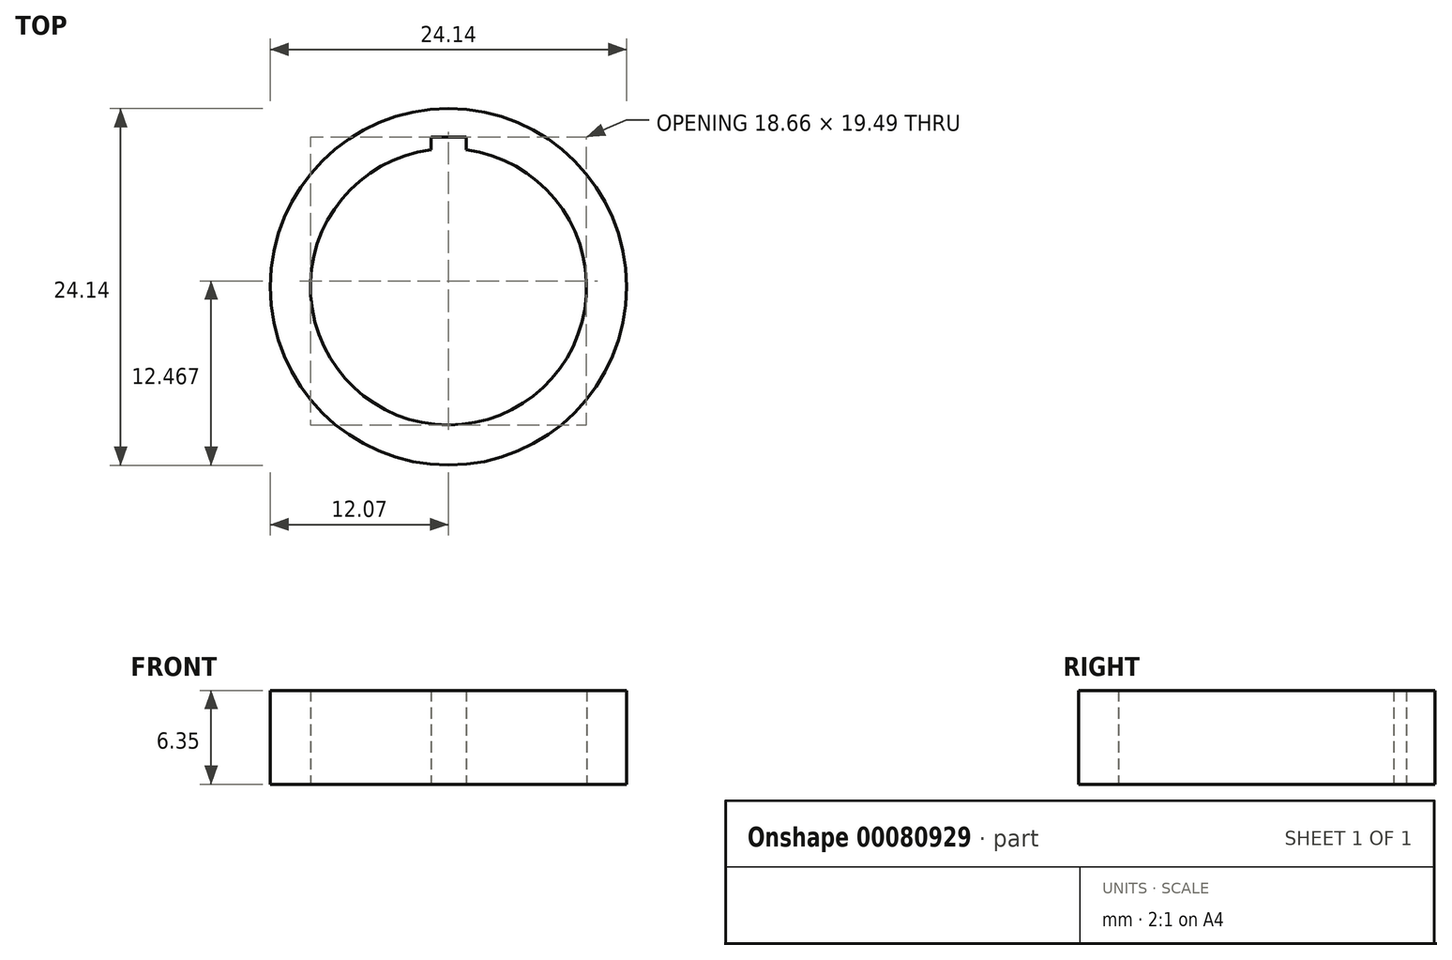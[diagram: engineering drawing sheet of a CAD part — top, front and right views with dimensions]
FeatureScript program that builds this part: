
annotation { "Feature Type Name" : "Feature", "Feature Type Description" : "" }
export const myFeature = defineFeature(function(context is Context, id is Id, definition is map)
    precondition{}
    {
        {
            var Q0;
            Q0=qCreatedBy(makeId("Top.planeOp"),FACE);
            var sketch = newSketch(context, id + "F0", { "sketchPlane" : qUnion([Q0])});
            skCircle(sketch, "E0", {"center": v(0, 0) * mm, "radius": 12.07 * mm});
            skCircle(sketch, "E1", {"center": v(0, 0) * mm, "radius": 9.35 * mm});
            skLineSegment(sketch, "E2.bottom", {"start": v(-1.2, 0) * mm, "end": v(1.2, 0) * mm});
            skLineSegment(sketch, "E2.top", {"start": v(-1.2, 10.14) * mm, "end": v(1.2, 10.14) * mm});
            skLineSegment(sketch, "E2.left", {"start": v(-1.2, 0) * mm, "end": v(-1.2, 10.14) * mm});
            skLineSegment(sketch, "E2.right", {"start": v(1.2, 0) * mm, "end": v(1.2, 10.14) * mm});
            skSolve(sketch);
        }
        {
            var Q0;
            Q0=makeQuery(id+"F0.imprint","IMPRINT",FACE,{"disambiguationData":[TD([[makeQuery(id+"F0.imprint","IMPRINT",EDGE,{"derivedFrom":sQuery(id+"F0.wireOp",EDGE,"E0")}),1.0]])]});
            extrude(context, id + "F1", {"entities" : qUnion([Q0]), "depth" : 6.35 * mm});
        }
    });
